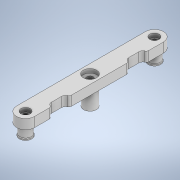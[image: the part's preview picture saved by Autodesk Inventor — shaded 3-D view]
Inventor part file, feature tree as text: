
AUTODESK INVENTOR PART (.ipt)
format: ipt  version: 2022.6 (Build 266554000, 554)  size: 233,984 bytes
history: native  units: mm
features: sketch x10, extrude x7, projected_geometry x7, fillet x4, hole x3, chamfer x1
ambient origin geometry x8: Origin, YZ Plane, XZ Plane, XY Plane, X Axis, Y Axis, Z Axis, Center Point
bodies: Solid1 (feature_tree)
feature tree (32):
  extrude  "Extrusion1"  Depth=7.0mm
  sketch  "Sketch2"  dims[d2=3.75mm d3=0.0mm d11=5.0mm]
  extrude  "Extrusion2"  Depth=3.75mm
  hole  "Hole2"  [1 undecoded]
  hole  "Hole3"  [1 undecoded]
  extrude  "Extrusion4"  Depth=3.0mm
  fillet  "Fillet1"  [1 undecoded]
  extrude  "Extrusion5"  Depth=3.0mm
  extrude  "Extrusion6"  Depth=3.0mm TaperAngle=0.0deg
  chamfer  "Chamfer1"  Distance=0.8mm
  fillet  "Fillet2"  Radius=2.0mm
  extrude  "Extrusion7"  Depth=10.0mm
  extrude  "Extrusion8"  Depth=10.0mm
  fillet  "Fillet3"  Radius=4.0mm
  fillet  "Fillet4"  Radius=4.8mm
  hole  "Hole4"  [1 undecoded]
  sketch  "Sketch1"  dims[d0=50.0mm d1=7.0mm]
  projected_geometry  "Projected Loop1"
  sketch  "Sketch3"  dims[d12=7.0mm d13=0.0mm d14=2.4mm]
  projected_geometry  "Projected Loop2"
  sketch  "Sketch5"  dims[d18=2.4mm d19=6.0mm d20=4.0mm d21=2.0mm d22=90.0deg d23=10.0mm d24=20.594885mm]
  sketch  "Sketch6"  dims[d25=5.2mm d26=6.0mm d27=4.0mm d28=2.0mm d29=90.0deg d30=1.5mm d31=0.0mm d32=4.0mm]
  sketch  "Sketch8"  dims[d33=3.0mm d34=15.0mm d35=0.0mm d36=0.0mm]
  projected_geometry  "Projected Loop4"
  sketch  "Sketch9"  dims[d37=1.0mm d38=3.0mm]
  projected_geometry  "Projected Loop5"
  sketch  "Sketch10"  dims[d39=3.0mm d40=5.8mm d41=0.0mm]
  sketch  "Sketch11"  dims[d42=3.7mm]
  projected_geometry  "Projected Loop6"
  projected_geometry  "Projected Loop7"
  sketch  "Sketch13"  dims[d43=3.7mm d44=0.8mm d45=0.0mm d46=0.3mm d47=2.0mm d48=45.0deg d49=0.5mm d50=4.5mm d52=4.0mm d53=0.0mm d54=4.8mm d56=0.4mm d57=0.0mm d61=0.4mm d62=0.8mm d63=2.2mm d64=6.0mm d65=3.6mm d66=1.5mm d67=90.0deg d68=10.0mm d69=20.594885mm d70=4.5mm]
  projected_geometry  "Projected Loop10"
note: 4 required parameter values undecoded (feature->parameter linkage not recoverable at this tier; creation-order binding heuristic only, values carry confidence <= 0.55)
